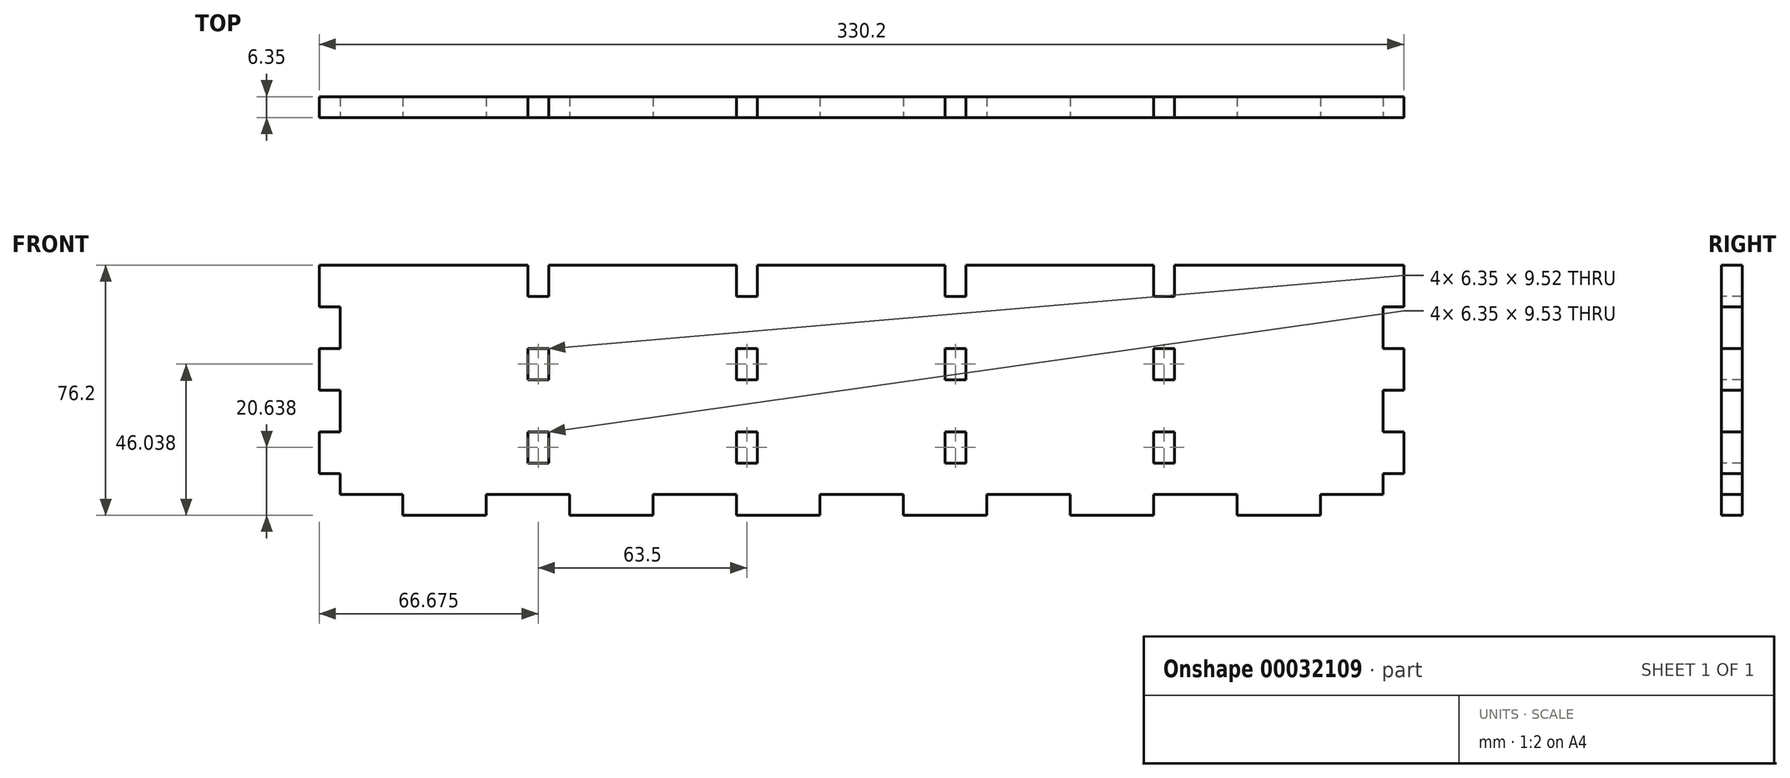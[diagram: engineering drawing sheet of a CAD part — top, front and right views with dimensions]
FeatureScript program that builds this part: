
annotation { "Feature Type Name" : "Feature", "Feature Type Description" : "" }
export const myFeature = defineFeature(function(context is Context, id is Id, definition is map)
    precondition{}
    {
        {
            var Q0;
            Q0=qCreatedBy(makeId("Front.planeOp"),FACE);
            var sketch = newSketch(context, id + "F0", { "sketchPlane" : qUnion([Q0])});
            skLineSegment(sketch, "E0.rect.bottom", {"start": v(-165.1, 38.1) * mm, "end": v(165.1, 38.1) * mm});
            skLineSegment(sketch, "E0.rect.top", {"start": v(-165.1, -38.1) * mm, "end": v(165.1, -38.1) * mm});
            skLineSegment(sketch, "E0.rect.left", {"start": v(-165.1, 38.1) * mm, "end": v(-165.1, -38.1) * mm});
            skLineSegment(sketch, "E0.rect.right", {"start": v(165.1, 38.1) * mm, "end": v(165.1, -38.1) * mm});
            skPoint(sketch, "E0.rect.middle", {"position": v(0, 0) * mm});
            skSolve(sketch);
        }
        {
            var Q0;
            Q0=makeQuery(id+"F0.imprint","IMPRINT",FACE,{"disambiguationData":[TD([[makeQuery(id+"F0.imprint","IMPRINT",EDGE,{"derivedFrom":sQuery(id+"F0.wireOp",EDGE,"E0.rect.bottom")}),-1.0]])]});
            extrude(context, id + "F1", {"entities" : qUnion([Q0]), "depth" : 6.35 * mm});
        }
        {
            var Q0;
            Q0=makeQuery(id+"F1.opExtrude","CAP_FACE",FACE,{"disambiguationData":[OSD([sQuery(id+"F0.wireOp",EDGE,"E0.rect.bottom"),sQuery(id+"F0.wireOp",EDGE,"E0.rect.top"),sQuery(id+"F0.wireOp",EDGE,"E0.rect.left"),sQuery(id+"F0.wireOp",EDGE,"E0.rect.right")])],"isStart":false});
            var sketch = newSketch(context, id + "F2", { "sketchPlane" : qUnion([Q0])});
            skLineSegment(sketch, "E1.bottom", {"start": v(-165.1, -38.1) * mm, "end": v(-139.7, -38.1) * mm});
            skLineSegment(sketch, "E1.top", {"start": v(-165.1, -31.75) * mm, "end": v(-139.7, -31.75) * mm});
            skLineSegment(sketch, "E1.left", {"start": v(-165.1, -38.1) * mm, "end": v(-165.1, -31.75) * mm});
            skLineSegment(sketch, "E1.right", {"start": v(-139.7, -38.1) * mm, "end": v(-139.7, -31.75) * mm});
            skLineSegment(sketch, "E2.1.0.0", {"start": v(-114.3, -31.75) * mm, "end": v(-88.9, -31.75) * mm});
            skLineSegment(sketch, "E2.1.0.1", {"start": v(-88.9, -38.1) * mm, "end": v(-88.9, -31.75) * mm});
            skLineSegment(sketch, "E2.1.0.2", {"start": v(-114.3, -38.1) * mm, "end": v(-88.9, -38.1) * mm});
            skLineSegment(sketch, "E2.1.0.3", {"start": v(-114.3, -38.1) * mm, "end": v(-114.3, -31.75) * mm});
            skLineSegment(sketch, "E2.2.0.0", {"start": v(-63.5, -31.75) * mm, "end": v(-38.1, -31.75) * mm});
            skLineSegment(sketch, "E2.2.0.1", {"start": v(-38.1, -38.1) * mm, "end": v(-38.1, -31.75) * mm});
            skLineSegment(sketch, "E2.2.0.2", {"start": v(-63.5, -38.1) * mm, "end": v(-38.1, -38.1) * mm});
            skLineSegment(sketch, "E2.2.0.3", {"start": v(-63.5, -38.1) * mm, "end": v(-63.5, -31.75) * mm});
            skLineSegment(sketch, "E2.3.0.0", {"start": v(-12.7, -31.75) * mm, "end": v(12.7, -31.75) * mm});
            skLineSegment(sketch, "E2.3.0.1", {"start": v(12.7, -38.1) * mm, "end": v(12.7, -31.75) * mm});
            skLineSegment(sketch, "E2.3.0.2", {"start": v(-12.7, -38.1) * mm, "end": v(12.7, -38.1) * mm});
            skLineSegment(sketch, "E2.3.0.3", {"start": v(-12.7, -38.1) * mm, "end": v(-12.7, -31.75) * mm});
            skLineSegment(sketch, "E2.4.0.0", {"start": v(38.1, -31.75) * mm, "end": v(63.5, -31.75) * mm});
            skLineSegment(sketch, "E2.4.0.1", {"start": v(63.5, -38.1) * mm, "end": v(63.5, -31.75) * mm});
            skLineSegment(sketch, "E2.4.0.2", {"start": v(38.1, -38.1) * mm, "end": v(63.5, -38.1) * mm});
            skLineSegment(sketch, "E2.4.0.3", {"start": v(38.1, -38.1) * mm, "end": v(38.1, -31.75) * mm});
            skLineSegment(sketch, "E2.5.0.0", {"start": v(88.9, -31.75) * mm, "end": v(114.3, -31.75) * mm});
            skLineSegment(sketch, "E2.5.0.1", {"start": v(114.3, -38.1) * mm, "end": v(114.3, -31.75) * mm});
            skLineSegment(sketch, "E2.5.0.2", {"start": v(88.9, -38.1) * mm, "end": v(114.3, -38.1) * mm});
            skLineSegment(sketch, "E2.5.0.3", {"start": v(88.9, -38.1) * mm, "end": v(88.9, -31.75) * mm});
            skLineSegment(sketch, "E2.6.0.0", {"start": v(139.7, -31.75) * mm, "end": v(165.1, -31.75) * mm});
            skLineSegment(sketch, "E2.6.0.1", {"start": v(165.1, -38.1) * mm, "end": v(165.1, -31.75) * mm});
            skLineSegment(sketch, "E2.6.0.2", {"start": v(139.7, -38.1) * mm, "end": v(165.1, -38.1) * mm});
            skLineSegment(sketch, "E2.6.0.3", {"start": v(139.7, -38.1) * mm, "end": v(139.7, -31.75) * mm});
            skLineSegment(sketch, "E2.direction1", {"start": v(-165.1, -31.75) * mm, "end": v(-114.3, -31.75) * mm, "construction": true});
            skLineSegment(sketch, "E3.bottom", {"start": v(-165.1, -12.7) * mm, "end": v(-158.75, -12.7) * mm});
            skLineSegment(sketch, "E3.top", {"start": v(-165.1, 0) * mm, "end": v(-158.75, 0) * mm});
            skLineSegment(sketch, "E3.left", {"start": v(-165.1, -12.7) * mm, "end": v(-165.1, 0) * mm});
            skLineSegment(sketch, "E3.right", {"start": v(-158.75, -12.7) * mm, "end": v(-158.75, 0) * mm});
            skLineSegment(sketch, "E4.bottom", {"start": v(-165.1, 25.4) * mm, "end": v(-158.75, 25.4) * mm});
            skLineSegment(sketch, "E4.top", {"start": v(-165.1, 12.7) * mm, "end": v(-158.75, 12.7) * mm});
            skLineSegment(sketch, "E4.left", {"start": v(-165.1, 25.4) * mm, "end": v(-165.1, 12.7) * mm});
            skLineSegment(sketch, "E4.right", {"start": v(-158.75, 25.4) * mm, "end": v(-158.75, 12.7) * mm});
            skLineSegment(sketch, "E5", {"start": v(0, -38.1) * mm, "end": v(0, 38.1) * mm, "construction": true});
            skLineSegment(sketch, "E6.MirrorCS", {"start": v(165.1, 25.4) * mm, "end": v(165.1, 12.7) * mm});
            skLineSegment(sketch, "E7.MirrorCS", {"start": v(165.1, 25.4) * mm, "end": v(158.75, 25.4) * mm});
            skLineSegment(sketch, "E8.MirrorCS", {"start": v(158.75, 25.4) * mm, "end": v(158.75, 12.7) * mm});
            skLineSegment(sketch, "E9.MirrorCS", {"start": v(165.1, -12.7) * mm, "end": v(158.75, -12.7) * mm});
            skLineSegment(sketch, "E10.MirrorCS", {"start": v(165.1, -12.7) * mm, "end": v(165.1, 0) * mm});
            skLineSegment(sketch, "E11.MirrorCS", {"start": v(158.75, -12.7) * mm, "end": v(158.75, 0) * mm});
            skLineSegment(sketch, "E12.MirrorCS", {"start": v(165.1, 0) * mm, "end": v(158.75, 0) * mm});
            skLineSegment(sketch, "E13.MirrorCS", {"start": v(165.1, 12.7) * mm, "end": v(158.75, 12.7) * mm});
            skSolve(sketch);
        }
        {
            var Q0;
            Q0 = qSketchRegion(id + "F2", true);
            extrude(context, id + "F3", {"entities" : qUnion([Q0]), "operationType" : NewBodyOperationType.REMOVE, "endBound" : BoundingType.UP_TO_NEXT, "oppositeDirection" : true, "depth" : 25.4 * mm});
        }
        {
            var Q0;
            Q0=makeQuery(id+"F1.opExtrude","CAP_FACE",FACE,{"disambiguationData":[OSD([sQuery(id+"F0.wireOp",EDGE,"E0.rect.bottom"),sQuery(id+"F0.wireOp",EDGE,"E0.rect.top"),sQuery(id+"F0.wireOp",EDGE,"E0.rect.left"),sQuery(id+"F0.wireOp",EDGE,"E0.rect.right")])],"isStart":false});
            var sketch = newSketch(context, id + "F4", { "sketchPlane" : qUnion([Q0])});
            skLineSegment(sketch, "E14.bottom", {"start": v(-101.6, 38.1) * mm, "end": v(-95.25, 38.1) * mm});
            skLineSegment(sketch, "E14.top", {"start": v(-101.6, 28.57) * mm, "end": v(-95.25, 28.57) * mm});
            skLineSegment(sketch, "E14.left", {"start": v(-101.6, 38.1) * mm, "end": v(-101.6, 28.57) * mm});
            skLineSegment(sketch, "E14.right", {"start": v(-95.25, 38.1) * mm, "end": v(-95.25, 28.57) * mm});
            skPoint(sketch, "E15", {"position": v(-98.43, 28.57) * mm});
            skPoint(sketch, "E16", {"position": v(-161.93, -12.7) * mm});
            skLineSegment(sketch, "E17.0.1.0", {"start": v(-95.25, 12.7) * mm, "end": v(-95.25, 3.17) * mm});
            skLineSegment(sketch, "E17.0.1.1", {"start": v(-101.6, 12.7) * mm, "end": v(-101.6, 3.17) * mm});
            skLineSegment(sketch, "E17.0.1.2", {"start": v(-101.6, 12.7) * mm, "end": v(-95.25, 12.7) * mm});
            skPoint(sketch, "E17.0.1.3", {"position": v(-98.43, 3.17) * mm});
            skLineSegment(sketch, "E17.0.1.4", {"start": v(-101.6, 3.17) * mm, "end": v(-95.25, 3.17) * mm});
            skLineSegment(sketch, "E17.1.0.0", {"start": v(-31.75, 38.1) * mm, "end": v(-31.75, 28.57) * mm});
            skLineSegment(sketch, "E17.1.0.1", {"start": v(-38.1, 38.1) * mm, "end": v(-38.1, 28.57) * mm});
            skLineSegment(sketch, "E17.1.0.2", {"start": v(-38.1, 38.1) * mm, "end": v(-31.75, 38.1) * mm});
            skPoint(sketch, "E17.1.0.3", {"position": v(-34.93, 28.57) * mm});
            skLineSegment(sketch, "E17.1.0.4", {"start": v(-38.1, 28.57) * mm, "end": v(-31.75, 28.57) * mm});
            skLineSegment(sketch, "E17.1.1.0", {"start": v(-31.75, 12.7) * mm, "end": v(-31.75, 3.17) * mm});
            skLineSegment(sketch, "E17.1.1.1", {"start": v(-38.1, 12.7) * mm, "end": v(-38.1, 3.17) * mm});
            skLineSegment(sketch, "E17.1.1.2", {"start": v(-38.1, 12.7) * mm, "end": v(-31.75, 12.7) * mm});
            skPoint(sketch, "E17.1.1.3", {"position": v(-34.93, 3.17) * mm});
            skLineSegment(sketch, "E17.1.1.4", {"start": v(-38.1, 3.17) * mm, "end": v(-31.75, 3.17) * mm});
            skLineSegment(sketch, "E17.2.0.0", {"start": v(31.75, 38.1) * mm, "end": v(31.75, 28.57) * mm});
            skLineSegment(sketch, "E17.2.0.1", {"start": v(25.4, 38.1) * mm, "end": v(25.4, 28.57) * mm});
            skLineSegment(sketch, "E17.2.0.2", {"start": v(25.4, 38.1) * mm, "end": v(31.75, 38.1) * mm});
            skPoint(sketch, "E17.2.0.3", {"position": v(28.57, 28.57) * mm});
            skLineSegment(sketch, "E17.2.0.4", {"start": v(25.4, 28.57) * mm, "end": v(31.75, 28.57) * mm});
            skLineSegment(sketch, "E17.2.1.0", {"start": v(31.75, 12.7) * mm, "end": v(31.75, 3.17) * mm});
            skLineSegment(sketch, "E17.2.1.1", {"start": v(25.4, 12.7) * mm, "end": v(25.4, 3.17) * mm});
            skLineSegment(sketch, "E17.2.1.2", {"start": v(25.4, 12.7) * mm, "end": v(31.75, 12.7) * mm});
            skPoint(sketch, "E17.2.1.3", {"position": v(28.57, 3.17) * mm});
            skLineSegment(sketch, "E17.2.1.4", {"start": v(25.4, 3.17) * mm, "end": v(31.75, 3.17) * mm});
            skLineSegment(sketch, "E17.3.0.0", {"start": v(95.25, 38.1) * mm, "end": v(95.25, 28.57) * mm});
            skLineSegment(sketch, "E17.3.0.1", {"start": v(88.9, 38.1) * mm, "end": v(88.9, 28.57) * mm});
            skLineSegment(sketch, "E17.3.0.2", {"start": v(88.9, 38.1) * mm, "end": v(95.25, 38.1) * mm});
            skPoint(sketch, "E17.3.0.3", {"position": v(92.07, 28.57) * mm});
            skLineSegment(sketch, "E17.3.0.4", {"start": v(88.9, 28.57) * mm, "end": v(95.25, 28.57) * mm});
            skLineSegment(sketch, "E17.3.1.0", {"start": v(95.25, 12.7) * mm, "end": v(95.25, 3.17) * mm});
            skLineSegment(sketch, "E17.3.1.1", {"start": v(88.9, 12.7) * mm, "end": v(88.9, 3.17) * mm});
            skLineSegment(sketch, "E17.3.1.2", {"start": v(88.9, 12.7) * mm, "end": v(95.25, 12.7) * mm});
            skPoint(sketch, "E17.3.1.3", {"position": v(92.07, 3.17) * mm});
            skLineSegment(sketch, "E17.3.1.4", {"start": v(88.9, 3.17) * mm, "end": v(95.25, 3.17) * mm});
            skLineSegment(sketch, "E17.direction1", {"start": v(-95.25, 28.57) * mm, "end": v(-31.75, 28.57) * mm, "construction": true});
            skLineSegment(sketch, "E17.direction2", {"start": v(-95.25, 28.57) * mm, "end": v(-95.25, 3.17) * mm, "construction": true});
            skLineSegment(sketch, "E18.0.0.2", {"start": v(-95.25, -12.7) * mm, "end": v(-95.25, -22.23) * mm});
            skLineSegment(sketch, "E18.3.0.2", {"start": v(-101.6, -12.7) * mm, "end": v(-101.6, -22.23) * mm});
            skLineSegment(sketch, "E18.6.0.2", {"start": v(-101.6, -12.7) * mm, "end": v(-95.25, -12.7) * mm});
            skPoint(sketch, "E18.9.0.2", {"position": v(-98.43, -22.23) * mm});
            skLineSegment(sketch, "E18.10.0.2", {"start": v(-101.6, -22.23) * mm, "end": v(-95.25, -22.23) * mm});
            skLineSegment(sketch, "E18.0.1.2", {"start": v(-31.75, -12.7) * mm, "end": v(-31.75, -22.23) * mm});
            skLineSegment(sketch, "E18.3.1.2", {"start": v(-38.1, -12.7) * mm, "end": v(-38.1, -22.23) * mm});
            skLineSegment(sketch, "E18.6.1.2", {"start": v(-38.1, -12.7) * mm, "end": v(-31.75, -12.7) * mm});
            skPoint(sketch, "E18.9.1.2", {"position": v(-34.93, -22.23) * mm});
            skLineSegment(sketch, "E18.10.1.2", {"start": v(-38.1, -22.23) * mm, "end": v(-31.75, -22.23) * mm});
            skLineSegment(sketch, "E18.0.2.2", {"start": v(31.75, -12.7) * mm, "end": v(31.75, -22.23) * mm});
            skLineSegment(sketch, "E18.3.2.2", {"start": v(25.4, -12.7) * mm, "end": v(25.4, -22.23) * mm});
            skLineSegment(sketch, "E18.6.2.2", {"start": v(25.4, -12.7) * mm, "end": v(31.75, -12.7) * mm});
            skPoint(sketch, "E18.9.2.2", {"position": v(28.57, -22.23) * mm});
            skLineSegment(sketch, "E18.10.2.2", {"start": v(25.4, -22.23) * mm, "end": v(31.75, -22.23) * mm});
            skLineSegment(sketch, "E18.0.3.2", {"start": v(95.25, -12.7) * mm, "end": v(95.25, -22.23) * mm});
            skLineSegment(sketch, "E18.3.3.2", {"start": v(88.9, -12.7) * mm, "end": v(88.9, -22.23) * mm});
            skLineSegment(sketch, "E18.6.3.2", {"start": v(88.9, -12.7) * mm, "end": v(95.25, -12.7) * mm});
            skPoint(sketch, "E18.9.3.2", {"position": v(92.07, -22.23) * mm});
            skLineSegment(sketch, "E18.10.3.2", {"start": v(88.9, -22.23) * mm, "end": v(95.25, -22.23) * mm});
            skSolve(sketch);
        }
        {
            var Q0;
            Q0=makeQuery(id+"F4.imprint","IMPRINT",FACE,{"disambiguationData":[TD([[makeQuery(id+"F4.imprint","IMPRINT",EDGE,{"derivedFrom":sQuery(id+"F4.wireOp",EDGE,"E14.bottom")}),-1.0]])]});
            var Q1;
            Q1=makeQuery(id+"F4.imprint","IMPRINT",FACE,{"disambiguationData":[TD([[makeQuery(id+"F4.imprint","IMPRINT",EDGE,{"derivedFrom":sQuery(id+"F4.wireOp",EDGE,"E17.0.1.0")}),-1.0]])]});
            var Q2;
            Q2=makeQuery(id+"F4.imprint","IMPRINT",FACE,{"disambiguationData":[TD([[makeQuery(id+"F4.imprint","IMPRINT",EDGE,{"derivedFrom":sQuery(id+"F4.wireOp",EDGE,"E18.0.0.2")}),-1.0]])]});
            var Q3;
            Q3=makeQuery(id+"F4.imprint","IMPRINT",FACE,{"disambiguationData":[TD([[makeQuery(id+"F4.imprint","IMPRINT",EDGE,{"derivedFrom":sQuery(id+"F4.wireOp",EDGE,"E18.0.0.3")}),-1.0]])]});
            var Q4;
            Q4=makeQuery(id+"F4.imprint","IMPRINT",FACE,{"disambiguationData":[TD([[makeQuery(id+"F4.imprint","IMPRINT",EDGE,{"derivedFrom":sQuery(id+"F4.wireOp",EDGE,"E17.1.1.0")}),-1.0]])]});
            var Q5;
            Q5=makeQuery(id+"F4.imprint","IMPRINT",FACE,{"disambiguationData":[TD([[makeQuery(id+"F4.imprint","IMPRINT",EDGE,{"derivedFrom":sQuery(id+"F4.wireOp",EDGE,"E17.1.0.0")}),-1.0]])]});
            var Q6;
            Q6=makeQuery(id+"F4.imprint","IMPRINT",FACE,{"disambiguationData":[TD([[makeQuery(id+"F4.imprint","IMPRINT",EDGE,{"derivedFrom":sQuery(id+"F4.wireOp",EDGE,"E18.0.1.2")}),-1.0]])]});
            var Q7;
            Q7=makeQuery(id+"F4.imprint","IMPRINT",FACE,{"disambiguationData":[TD([[makeQuery(id+"F4.imprint","IMPRINT",EDGE,{"derivedFrom":sQuery(id+"F4.wireOp",EDGE,"E18.0.2.3")}),-1.0]])]});
            var Q8;
            Q8=makeQuery(id+"F4.imprint","IMPRINT",FACE,{"disambiguationData":[TD([[makeQuery(id+"F4.imprint","IMPRINT",EDGE,{"derivedFrom":sQuery(id+"F4.wireOp",EDGE,"E17.2.1.0")}),-1.0]])]});
            var Q9;
            Q9=makeQuery(id+"F4.imprint","IMPRINT",FACE,{"disambiguationData":[TD([[makeQuery(id+"F4.imprint","IMPRINT",EDGE,{"derivedFrom":sQuery(id+"F4.wireOp",EDGE,"E17.2.0.0")}),-1.0]])]});
            var Q10;
            Q10=makeQuery(id+"F4.imprint","IMPRINT",FACE,{"disambiguationData":[TD([[makeQuery(id+"F4.imprint","IMPRINT",EDGE,{"derivedFrom":sQuery(id+"F4.wireOp",EDGE,"E18.0.2.2")}),-1.0]])]});
            var Q11;
            Q11=makeQuery(id+"F4.imprint","IMPRINT",FACE,{"disambiguationData":[TD([[makeQuery(id+"F4.imprint","IMPRINT",EDGE,{"derivedFrom":sQuery(id+"F4.wireOp",EDGE,"E18.0.3.2")}),-1.0]])]});
            var Q12;
            Q12=makeQuery(id+"F4.imprint","IMPRINT",FACE,{"disambiguationData":[TD([[makeQuery(id+"F4.imprint","IMPRINT",EDGE,{"derivedFrom":sQuery(id+"F4.wireOp",EDGE,"E17.3.1.0")}),-1.0]])]});
            var Q13;
            Q13=makeQuery(id+"F4.imprint","IMPRINT",FACE,{"disambiguationData":[TD([[makeQuery(id+"F4.imprint","IMPRINT",EDGE,{"derivedFrom":sQuery(id+"F4.wireOp",EDGE,"E17.3.0.0")}),-1.0]])]});
            var Q14;
            Q14=makeQuery(id+"F4.imprint","IMPRINT",FACE,{"disambiguationData":[TD([[makeQuery(id+"F4.imprint","IMPRINT",EDGE,{"derivedFrom":sQuery(id+"F4.wireOp",EDGE,"E18.0.3.3")}),-1.0]])]});
            extrude(context, id + "F5", {"entities" : qUnion([Q0, Q1, Q2, Q3, Q4, Q5, Q6, Q7, Q8, Q9, Q10, Q11, Q12, Q13, Q14]), "operationType" : NewBodyOperationType.REMOVE, "endBound" : BoundingType.UP_TO_NEXT, "oppositeDirection" : true, "depth" : 25.4 * mm});
        }
        {
            var Q0;
            Q0=makeQuery(id+"F1.opExtrude","CAP_FACE",FACE,{"disambiguationData":[OSD([sQuery(id+"F0.wireOp",EDGE,"E0.rect.bottom"),sQuery(id+"F0.wireOp",EDGE,"E0.rect.top"),sQuery(id+"F0.wireOp",EDGE,"E0.rect.left"),sQuery(id+"F0.wireOp",EDGE,"E0.rect.right")])],"isStart":false});
            var sketch = newSketch(context, id + "F6", { "sketchPlane" : qUnion([Q0])});
            skPoint(sketch, "E19.oppositeSnap0", {"position": v(-158.75, -6.35) * mm});
            skLineSegment(sketch, "E19.bottom", {"start": v(-165.1, -31.75) * mm, "end": v(-158.75, -31.75) * mm});
            skLineSegment(sketch, "E19.top", {"start": v(-165.1, -25.4) * mm, "end": v(-158.75, -25.4) * mm});
            skLineSegment(sketch, "E19.left", {"start": v(-165.1, -31.75) * mm, "end": v(-165.1, -25.4) * mm});
            skLineSegment(sketch, "E19.right", {"start": v(-158.75, -31.75) * mm, "end": v(-158.75, -25.4) * mm});
            skLineSegment(sketch, "E20.bottom", {"start": v(165.1, -31.75) * mm, "end": v(158.75, -31.75) * mm});
            skLineSegment(sketch, "E20.top", {"start": v(165.1, -25.4) * mm, "end": v(158.75, -25.4) * mm});
            skLineSegment(sketch, "E20.left", {"start": v(165.1, -31.75) * mm, "end": v(165.1, -25.4) * mm});
            skLineSegment(sketch, "E20.right", {"start": v(158.75, -31.75) * mm, "end": v(158.75, -25.4) * mm});
            skSolve(sketch);
        }
        {
            var Q0;
            Q0 = qSketchRegion(id + "F6", true);
            extrude(context, id + "F7", {"entities" : qUnion([Q0]), "operationType" : NewBodyOperationType.REMOVE, "endBound" : BoundingType.UP_TO_NEXT, "oppositeDirection" : true, "depth" : 25.4 * mm});
        }
    });
